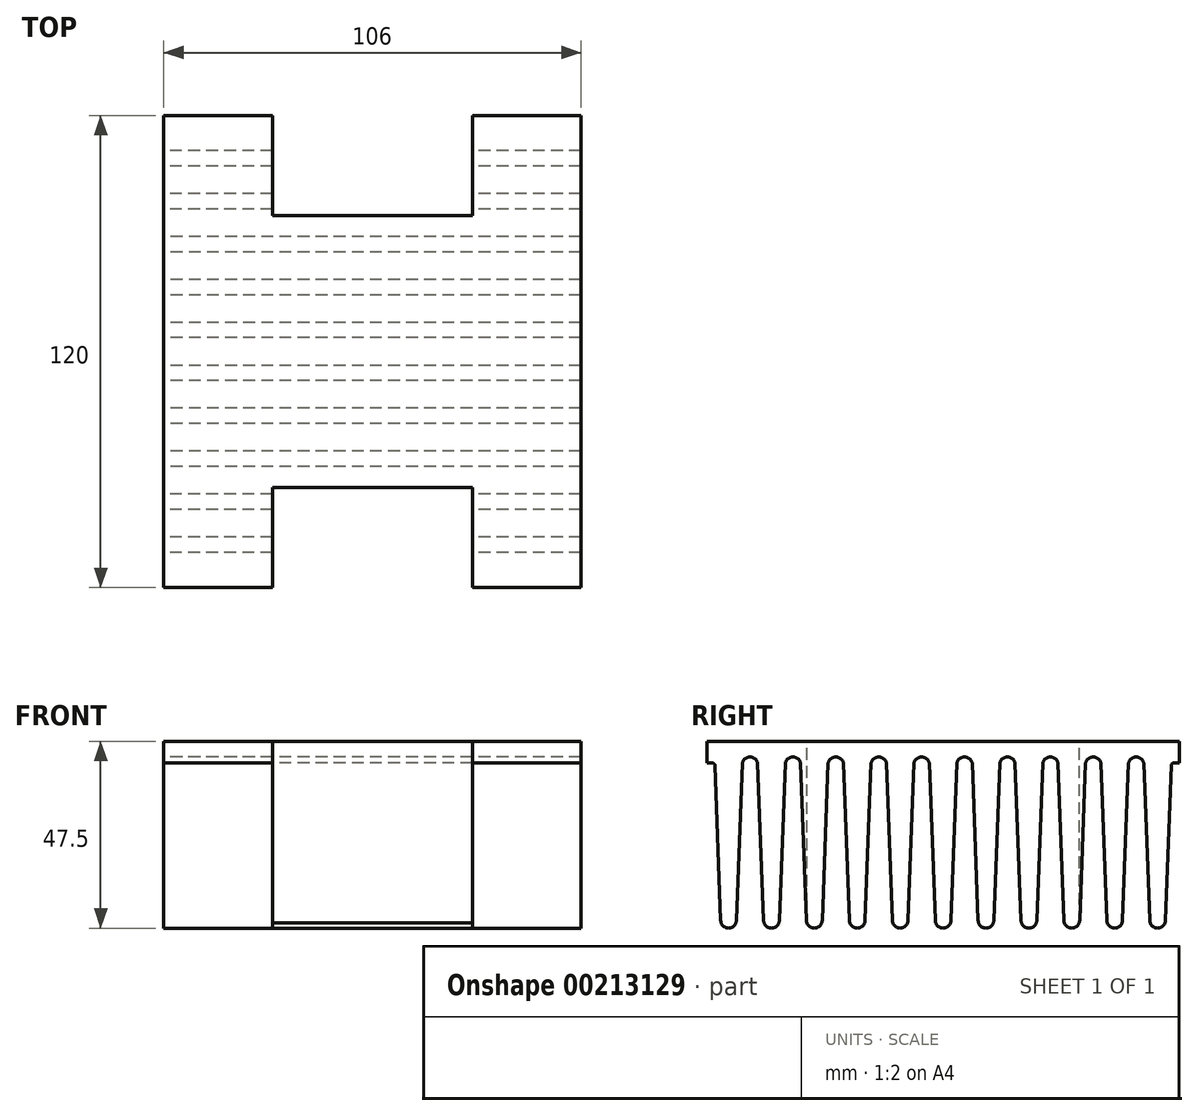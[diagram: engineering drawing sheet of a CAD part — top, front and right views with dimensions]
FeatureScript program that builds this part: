
annotation { "Feature Type Name" : "Feature", "Feature Type Description" : "" }
export const myFeature = defineFeature(function(context is Context, id is Id, definition is map)
    precondition{}
    {
        {
            var Q0;
            Q0=qCreatedBy(makeId("Right.planeOp"),FACE);
            var sketch = newSketch(context, id + "F0", { "sketchPlane" : qUnion([Q0])});
            skLineSegment(sketch, "E0", {"start": v(-57.86, 13.27) * mm, "end": v(62.14, 13.27) * mm});
            skLineSegment(sketch, "E1", {"start": v(62.14, 13.27) * mm, "end": v(62.14, 7.7) * mm});
            skLineSegment(sketch, "E2", {"start": v(-56.42, 7.7) * mm, "end": v(-57.86, 7.7) * mm, "construction": true});
            skLineSegment(sketch, "E3", {"start": v(-57.86, 7.7) * mm, "end": v(-57.86, 13.27) * mm});
            skLineSegment(sketch, "E4", {"start": v(-55.86, 7.7) * mm, "end": v(-48.86, 7.7) * mm, "construction": true});
            skLineSegment(sketch, "E5", {"start": v(-48.86, 7.7) * mm, "end": v(-50.36, -32.3) * mm});
            skLineSegment(sketch, "E6", {"start": v(-52.36, 7.7) * mm, "end": v(-52.36, -32.3) * mm, "construction": true});
            skLineSegment(sketch, "E7", {"start": v(-55.84, 7.14) * mm, "end": v(-54.36, -32.3) * mm});
            skLineSegment(sketch, "E8.1.0.0", {"start": v(-44.96, 7.7) * mm, "end": v(-43.46, -32.3) * mm});
            skLineSegment(sketch, "E8.1.0.2", {"start": v(-37.96, 7.7) * mm, "end": v(-39.46, -32.3) * mm});
            skLineSegment(sketch, "E8.2.0.0", {"start": v(-34.06, 7.7) * mm, "end": v(-32.56, -32.3) * mm});
            skLineSegment(sketch, "E8.2.0.2", {"start": v(-27.06, 7.7) * mm, "end": v(-28.56, -32.3) * mm});
            skLineSegment(sketch, "E8.3.0.0", {"start": v(-23.16, 7.7) * mm, "end": v(-21.66, -32.3) * mm});
            skLineSegment(sketch, "E8.3.0.2", {"start": v(-16.16, 7.7) * mm, "end": v(-17.66, -32.3) * mm});
            skLineSegment(sketch, "E8.4.0.0", {"start": v(-12.26, 7.7) * mm, "end": v(-10.76, -32.3) * mm});
            skLineSegment(sketch, "E8.4.0.2", {"start": v(-5.26, 7.7) * mm, "end": v(-6.76, -32.3) * mm});
            skLineSegment(sketch, "E8.5.0.0", {"start": v(-1.36, 7.7) * mm, "end": v(0.14, -32.3) * mm});
            skLineSegment(sketch, "E8.5.0.2", {"start": v(5.64, 7.7) * mm, "end": v(4.14, -32.3) * mm});
            skLineSegment(sketch, "E8.6.0.0", {"start": v(9.54, 7.7) * mm, "end": v(11.04, -32.3) * mm});
            skLineSegment(sketch, "E8.6.0.2", {"start": v(16.54, 7.7) * mm, "end": v(15.04, -32.3) * mm});
            skLineSegment(sketch, "E8.7.0.0", {"start": v(20.44, 7.7) * mm, "end": v(21.94, -32.3) * mm});
            skLineSegment(sketch, "E8.7.0.2", {"start": v(27.44, 7.7) * mm, "end": v(25.94, -32.3) * mm});
            skLineSegment(sketch, "E8.8.0.0", {"start": v(31.34, 7.7) * mm, "end": v(32.84, -32.3) * mm});
            skLineSegment(sketch, "E8.8.0.2", {"start": v(38.34, 7.7) * mm, "end": v(36.84, -32.3) * mm});
            skLineSegment(sketch, "E8.9.0.0", {"start": v(42.24, 7.7) * mm, "end": v(43.74, -32.3) * mm});
            skLineSegment(sketch, "E8.9.0.2", {"start": v(49.24, 7.7) * mm, "end": v(47.74, -32.3) * mm});
            skLineSegment(sketch, "E8.10.0.0", {"start": v(53.14, 7.7) * mm, "end": v(54.64, -32.3) * mm});
            skLineSegment(sketch, "E8.10.0.2", {"start": v(60.12, 7.14) * mm, "end": v(58.64, -32.3) * mm});
            skLineSegment(sketch, "E8.direction1", {"start": v(-50.36, -32.3) * mm, "end": v(-43.46, -32.3) * mm, "construction": true});
            skLineSegment(sketch, "E9", {"start": v(60.7, 7.7) * mm, "end": v(62.14, 7.7) * mm});
            skArc(sketch, "E10", {"start": v(-54.36, -32.3) * mm, "mid": v(-52.36, -34.23) * mm, "end": v(-50.36, -32.3) * mm});
            skArc(sketch, "E11", {"start": v(-44.96, 7.7) * mm, "mid": v(-46.91, 9.25) * mm, "end": v(-48.86, 7.7) * mm});
            skArc(sketch, "E12.1.0.0", {"start": v(-34.06, 7.7) * mm, "mid": v(-36.01, 9.25) * mm, "end": v(-37.96, 7.7) * mm});
            skArc(sketch, "E12.1.0.1", {"start": v(-43.46, -32.3) * mm, "mid": v(-41.46, -34.23) * mm, "end": v(-39.46, -32.3) * mm});
            skArc(sketch, "E12.2.0.0", {"start": v(-23.16, 7.7) * mm, "mid": v(-25.11, 9.25) * mm, "end": v(-27.06, 7.7) * mm});
            skArc(sketch, "E12.2.0.1", {"start": v(-32.56, -32.3) * mm, "mid": v(-30.56, -34.23) * mm, "end": v(-28.56, -32.3) * mm});
            skArc(sketch, "E12.3.0.0", {"start": v(-12.26, 7.7) * mm, "mid": v(-14.21, 9.25) * mm, "end": v(-16.16, 7.7) * mm});
            skArc(sketch, "E12.3.0.1", {"start": v(-21.66, -32.3) * mm, "mid": v(-19.66, -34.23) * mm, "end": v(-17.66, -32.3) * mm});
            skArc(sketch, "E12.4.0.0", {"start": v(-1.36, 7.7) * mm, "mid": v(-3.31, 9.25) * mm, "end": v(-5.26, 7.7) * mm});
            skArc(sketch, "E12.4.0.1", {"start": v(-10.76, -32.3) * mm, "mid": v(-8.76, -34.23) * mm, "end": v(-6.76, -32.3) * mm});
            skArc(sketch, "E12.5.0.0", {"start": v(9.54, 7.7) * mm, "mid": v(7.59, 9.25) * mm, "end": v(5.64, 7.7) * mm});
            skArc(sketch, "E12.5.0.1", {"start": v(0.14, -32.3) * mm, "mid": v(2.14, -34.23) * mm, "end": v(4.14, -32.3) * mm});
            skArc(sketch, "E12.6.0.0", {"start": v(20.44, 7.7) * mm, "mid": v(18.49, 9.25) * mm, "end": v(16.54, 7.7) * mm});
            skArc(sketch, "E12.6.0.1", {"start": v(11.04, -32.3) * mm, "mid": v(13.04, -34.23) * mm, "end": v(15.04, -32.3) * mm});
            skArc(sketch, "E12.7.0.0", {"start": v(31.34, 7.7) * mm, "mid": v(29.39, 9.25) * mm, "end": v(27.44, 7.7) * mm});
            skArc(sketch, "E12.7.0.1", {"start": v(21.94, -32.3) * mm, "mid": v(23.94, -34.23) * mm, "end": v(25.94, -32.3) * mm});
            skArc(sketch, "E12.8.0.0", {"start": v(42.24, 7.7) * mm, "mid": v(40.29, 9.25) * mm, "end": v(38.34, 7.7) * mm});
            skArc(sketch, "E12.8.0.1", {"start": v(32.84, -32.3) * mm, "mid": v(34.84, -34.23) * mm, "end": v(36.84, -32.3) * mm});
            skArc(sketch, "E12.9.0.0", {"start": v(53.14, 7.7) * mm, "mid": v(51.19, 9.25) * mm, "end": v(49.24, 7.7) * mm});
            skArc(sketch, "E12.9.0.1", {"start": v(43.74, -32.3) * mm, "mid": v(45.74, -34.23) * mm, "end": v(47.74, -32.3) * mm});
            skArc(sketch, "E12.10.0.1", {"start": v(54.64, -32.3) * mm, "mid": v(56.64, -34.23) * mm, "end": v(58.64, -32.3) * mm});
            skLineSegment(sketch, "E12.direction1", {"start": v(-48.86, 7.7) * mm, "end": v(-37.96, 7.7) * mm, "construction": true});
            skPoint(sketch, "E13.orphan", {"position": v(60.14, 7.7) * mm});
            skLineSegment(sketch, "E14", {"start": v(-57.86, 7.7) * mm, "end": v(-55.86, 7.7) * mm});
            skPoint(sketch, "E15.newPointA", {"position": v(-55.86, 7.7) * mm});
            skArc(sketch, "E15.filletArc", {"start": v(-55.84, 7.14) * mm, "mid": v(-56.02, 7.54) * mm, "end": v(-56.42, 7.7) * mm});
            skArc(sketch, "E16.filletArc", {"start": v(60.7, 7.7) * mm, "mid": v(60.3, 7.54) * mm, "end": v(60.12, 7.14) * mm});
            skSolve(sketch);
        }
        {
            var Q0;
            Q0 = qSketchRegion(id + "F0", true);
            extrude(context, id + "F1", {"entities" : qUnion([Q0]), "depth" : 130 * mm});
        }
        {
            var Q0;
            Q0=makeQuery(id+"FSTNRPARWx8Cywk_1.splitOp","SPLIT",FACE,{"derivedFrom":makeQuery(id+"FjCpp3TqFKTy6qa_1.splitOp","SPLIT",FACE,{"derivedFrom":makeQuery(id+"F1.opExtrude","SWEPT_FACE",FACE,{"disambiguationData":[OSD([sQuery(id+"F0.wireOp",EDGE,"E0")])]})}),"isFromBackBody":true});
            var sketch = newSketch(context, id + "F2", { "sketchPlane" : qUnion([Q0])});
            skPoint(sketch, "E17.orphan", {"position": v(93.89, 26.6) * mm});
            skPoint(sketch, "E18.orphan", {"position": v(93.89, -26.6) * mm});
            skPoint(sketch, "E19", {"position": v(65, -57.86) * mm});
            skPoint(sketch, "E20.orphan", {"position": v(65, -63.6) * mm});
            skLineSegment(sketch, "E21", {"start": v(39.6, -57.86) * mm, "end": v(39.6, -32.46) * mm});
            skLineSegment(sketch, "E22", {"start": v(90.4, -57.86) * mm, "end": v(90.4, -32.46) * mm});
            skLineSegment(sketch, "E23", {"start": v(90.4, -32.46) * mm, "end": v(39.6, -32.46) * mm});
            skLineSegment(sketch, "E24", {"start": v(39.6, -57.86) * mm, "end": v(90.4, -57.86) * mm});
            skLineSegment(sketch, "E25", {"start": v(39.6, 62.14) * mm, "end": v(39.6, 36.74) * mm});
            skLineSegment(sketch, "E26", {"start": v(39.6, 36.74) * mm, "end": v(90.4, 36.74) * mm});
            skLineSegment(sketch, "E27", {"start": v(90.4, 36.74) * mm, "end": v(90.4, 62.14) * mm});
            skLineSegment(sketch, "E28", {"start": v(90.4, 62.14) * mm, "end": v(39.6, 62.14) * mm});
            skSolve(sketch);
        }
        {
            var Q0;
            Q0 = qSketchRegion(id + "F2", true);
            var Q1;
            {var subQ0=sQuery(id+"F2.wireOp",EDGE,"1Z8Zt9HP-dKhJ-aCIr-bUaQ-vG37QqQZ94Kd");Q1=makeQuery(id+"F2.imprint","IMPRINT",FACE,{"disambiguationData":[TD([[makeQuery(id+"F2.imprint","IMPRINT",EDGE,{"derivedFrom":subQ0}),1.0]])]});}
            extrude(context, id + "F3", {"entities" : qUnion([Q0, Q1]), "operationType" : NewBodyOperationType.REMOVE, "oppositeDirection" : true, "depth" : 79.5 * mm});
        }
        {
            var Q0;
            Q0=makeQuery(id+"FSTNRPARWx8Cywk_1.splitOp","SPLIT",FACE,{"derivedFrom":makeQuery(id+"FjCpp3TqFKTy6qa_1.splitOp","SPLIT",FACE,{"derivedFrom":makeQuery(id+"F1.opExtrude","SWEPT_FACE",FACE,{"disambiguationData":[OSD([sQuery(id+"F0.wireOp",EDGE,"E0")])]})}),"isFromBackBody":true});
            var sketch = newSketch(context, id + "F4", { "sketchPlane" : qUnion([Q0])});
            skLineSegment(sketch, "E29", {"start": v(0, 11.54) * mm, "end": v(12, 11.54) * mm});
            skLineSegment(sketch, "E30", {"start": v(130, 10.99) * mm, "end": v(118, 10.99) * mm});
            skLineSegment(sketch, "E31.bottom", {"start": v(0, 62.24) * mm, "end": v(12, 62.24) * mm});
            skLineSegment(sketch, "E31.top", {"start": v(0, -58.24) * mm, "end": v(12, -58.24) * mm});
            skLineSegment(sketch, "E31.left", {"start": v(0, 62.24) * mm, "end": v(0, -58.24) * mm});
            skLineSegment(sketch, "E31.right", {"start": v(12, 62.24) * mm, "end": v(12, -58.24) * mm});
            skLineSegment(sketch, "E32.bottom", {"start": v(130, 63.34) * mm, "end": v(118, 63.34) * mm});
            skLineSegment(sketch, "E32.top", {"start": v(130, -58.9) * mm, "end": v(118, -58.9) * mm});
            skLineSegment(sketch, "E32.left", {"start": v(130, 63.34) * mm, "end": v(130, -58.9) * mm});
            skLineSegment(sketch, "E32.right", {"start": v(118, 63.34) * mm, "end": v(118, -58.9) * mm});
            skSolve(sketch);
        }
        {
            var Q0;
            Q0 = qSketchRegion(id + "F4", true);
            extrude(context, id + "F5", {"entities" : qUnion([Q0]), "operationType" : NewBodyOperationType.REMOVE, "endBound" : BoundingType.THROUGH_ALL, "oppositeDirection" : true, "depth" : 25 * mm});
        }
    });
